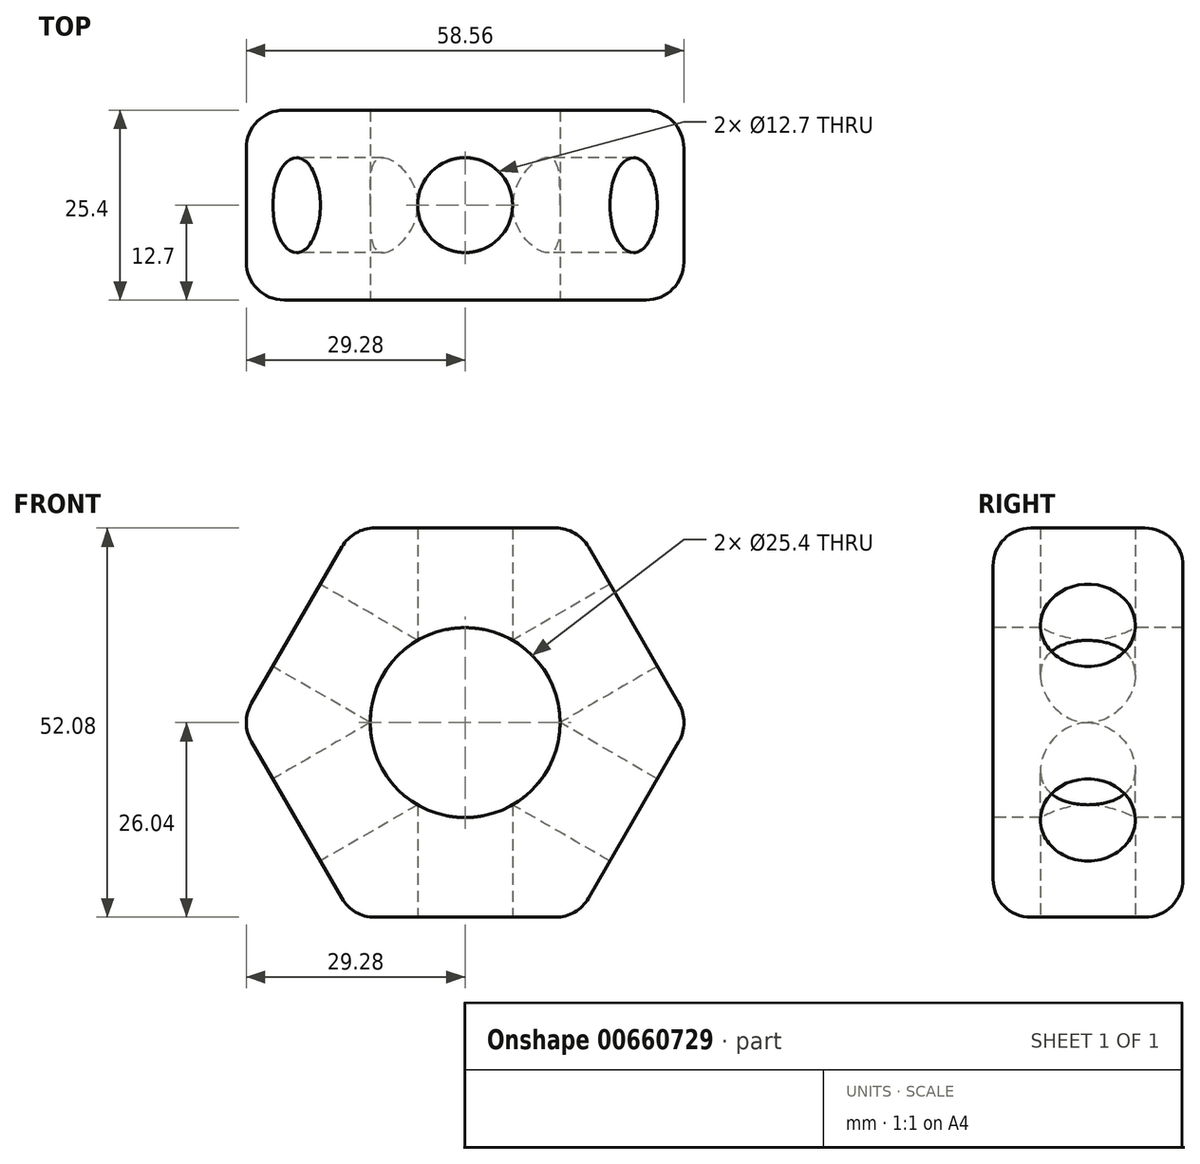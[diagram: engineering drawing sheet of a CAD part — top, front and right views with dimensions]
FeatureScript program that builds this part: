
annotation { "Feature Type Name" : "Feature", "Feature Type Description" : "" }
export const myFeature = defineFeature(function(context is Context, id is Id, definition is map)
    precondition{}
    {
        {
            var Q0;
            Q0=qCreatedBy(makeId("Front.planeOp"),FACE);
            var sketch = newSketch(context, id + "F0", { "sketchPlane" : qUnion([Q0])});
            skCircle(sketch, "E0", {"center": v(0, 0) * mm, "radius": 26.04 * mm});
            skCircle(sketch, "E1.cCircle", {"center": v(0, 0) * mm, "radius": 26.04 * mm, "construction": true});
            skLineSegment(sketch, "E1.0", {"start": v(-15.03, 26.04) * mm, "end": v(15.03, 26.04) * mm});
            skLineSegment(sketch, "E1.1", {"start": v(15.03, 26.04) * mm, "end": v(30.07, 0) * mm});
            skLineSegment(sketch, "E1.2", {"start": v(30.07, 0) * mm, "end": v(15.03, -26.04) * mm});
            skLineSegment(sketch, "E1.3", {"start": v(15.03, -26.04) * mm, "end": v(-15.03, -26.04) * mm});
            skLineSegment(sketch, "E1.4", {"start": v(-15.03, -26.04) * mm, "end": v(-30.07, 0) * mm});
            skLineSegment(sketch, "E1.5", {"start": v(-30.07, 0) * mm, "end": v(-15.03, 26.04) * mm});
            skPoint(sketch, "E1.0.midPoint", {"position": v(0, 26.04) * mm});
            skSolve(sketch);
        }
        {
            var Q0;
            Q0 = qSketchRegion(id + "F0", true);
            extrude(context, id + "F1", {"entities" : qUnion([Q0]), "endBound" : BoundingType.SYMMETRIC, "depth" : 25.4 * mm, "offsetDistance" : 25.4 * mm});
        }
        {
            var Q0;
            Q0=qCreatedBy(makeId("Front.planeOp"),FACE);
            var sketch = newSketch(context, id + "F2", { "sketchPlane" : qUnion([Q0])});
            skCircle(sketch, "E2", {"center": v(0, 0) * mm, "radius": 11.03 * mm});
            skSolve(sketch);
        }
        {
            var Q0;
            Q0=qCreatedBy(makeId("Front.planeOp"),FACE);
            var sketch = newSketch(context, id + "F3", { "sketchPlane" : qUnion([Q0])});
            skCircle(sketch, "E3", {"center": v(0, 0) * mm, "radius": 1.4 * mm});
            skSolve(sketch);
        }
        {
            var Q0;
            Q0=sQuery(id+"F3.wireOp",VERTEX,"E3.center");
            var Q1;
            Q1=makeQuery(id+"F1.opExtrude","SWEPT_BODY",BODY,{"disambiguationData":[OSD([sQuery(id+"F0.wireOp",EDGE,"E1.0"),sQuery(id+"F0.wireOp",EDGE,"E1.1"),sQuery(id+"F0.wireOp",EDGE,"E1.2"),sQuery(id+"F0.wireOp",EDGE,"E1.3"),sQuery(id+"F0.wireOp",EDGE,"E1.4"),sQuery(id+"F0.wireOp",EDGE,"E1.5")])]});
            hole(context, id + "F4", {"style" : HoleStyle.SIMPLE, "endStyle" : HoleEndStyle.THROUGH, "holeDiameter" : 25.4 * mm, "majorDiameter" : 6.35 * mm, "isTappedThrough" : true, "tappedDepth" : 12.7 * mm, "tapClearance" : 3, "locations" : qUnion([Q0]), "scope" : qUnion([Q1])});
        }
        {
            var Q0;
            Q0=sQuery(id+"F2.wireOp",VERTEX,"E2.center");
            var Q1;
            Q1=makeQuery(id+"F1.opExtrude","SWEPT_BODY",BODY,{"disambiguationData":[OSD([sQuery(id+"F0.wireOp",EDGE,"E1.0"),sQuery(id+"F0.wireOp",EDGE,"E1.1"),sQuery(id+"F0.wireOp",EDGE,"E1.2"),sQuery(id+"F0.wireOp",EDGE,"E1.3"),sQuery(id+"F0.wireOp",EDGE,"E1.4"),sQuery(id+"F0.wireOp",EDGE,"E1.5")])]});
            hole(context, id + "F5", {"style" : HoleStyle.SIMPLE, "endStyle" : HoleEndStyle.THROUGH, "oppositeDirection" : true, "holeDiameter" : 25.4 * mm, "majorDiameter" : 6.35 * mm, "isTappedThrough" : true, "tappedDepth" : 12.7 * mm, "tapClearance" : 3, "locations" : qUnion([Q0]), "scope" : qUnion([Q1])});
        }
        {
            var Q0;
            Q0=makeQuery(id+"F1.opExtrude","SWEPT_FACE",FACE,{"disambiguationData":[OSD([sQuery(id+"F0.wireOp",EDGE,"E1.5")])]});
            var sketch = newSketch(context, id + "F6", { "sketchPlane" : qUnion([Q0])});
            skPoint(sketch, "E4", {"position": v(0, 0) * mm});
            skSolve(sketch);
        }
        {
            var Q0;
            Q0=sQuery(id+"F6.wireOp",VERTEX,"E4");
            var Q1;
            Q1=makeQuery(id+"F1.opExtrude","SWEPT_BODY",BODY,{"disambiguationData":[OSD([sQuery(id+"F0.wireOp",EDGE,"E1.0"),sQuery(id+"F0.wireOp",EDGE,"E1.1"),sQuery(id+"F0.wireOp",EDGE,"E1.2"),sQuery(id+"F0.wireOp",EDGE,"E1.3"),sQuery(id+"F0.wireOp",EDGE,"E1.4"),sQuery(id+"F0.wireOp",EDGE,"E1.5")])]});
            hole(context, id + "F7", {"style" : HoleStyle.SIMPLE, "endStyle" : HoleEndStyle.THROUGH, "holeDiameter" : 12.7 * mm, "majorDiameter" : 5 * mm, "isTappedThrough" : true, "tappedDepth" : 12.7 * mm, "tapClearance" : 3, "locations" : qUnion([Q0]), "scope" : qUnion([Q1])});
        }
        {
            var Q0;
            Q0=makeQuery(id+"F1.opExtrude","SWEPT_EDGE",EDGE,{"disambiguationData":[OSD([sQuery(id+"F0.wireOp",EDGE,"E1.4"),sQuery(id+"F0.wireOp",EDGE,"E1.5")])]});
            fillet(context, id + "F8", {"entities" : qUnion([Q0]), "radius" : 5.08 * mm, "tangentPropagation" : true, "allowEdgeOverflow" : false});
        }
        {
            var Q0;
            Q0=makeQuery(id+"F1.opExtrude","SWEPT_EDGE",EDGE,{"disambiguationData":[OSD([sQuery(id+"F0.wireOp",EDGE,"E1.3"),sQuery(id+"F0.wireOp",EDGE,"E1.4")])]});
            var Q1;
            Q1=makeQuery(id+"F1.opExtrude","SWEPT_EDGE",EDGE,{"disambiguationData":[OSD([sQuery(id+"F0.wireOp",EDGE,"E1.0"),sQuery(id+"F0.wireOp",EDGE,"E1.5")])]});
            var Q2;
            Q2=makeQuery(id+"F1.opExtrude","SWEPT_EDGE",EDGE,{"disambiguationData":[OSD([sQuery(id+"F0.wireOp",EDGE,"E1.2"),sQuery(id+"F0.wireOp",EDGE,"E1.3")])]});
            var Q3;
            Q3=makeQuery(id+"F1.opExtrude","SWEPT_EDGE",EDGE,{"disambiguationData":[OSD([sQuery(id+"F0.wireOp",EDGE,"E1.1"),sQuery(id+"F0.wireOp",EDGE,"E1.2")])]});
            var Q4;
            Q4=makeQuery(id+"F1.opExtrude","SWEPT_EDGE",EDGE,{"disambiguationData":[OSD([sQuery(id+"F0.wireOp",EDGE,"E1.0"),sQuery(id+"F0.wireOp",EDGE,"E1.1")])]});
            fillet(context, id + "F9", {"entities" : qUnion([Q0, Q1, Q2, Q3, Q4]), "radius" : 5.08 * mm, "tangentPropagation" : true, "allowEdgeOverflow" : false});
        }
        {
            var Q0;
            Q0=makeQuery(id+"F9.opFillet","BLEND_FACE",FACE,{"disambiguationData":[OSD([sQuery(id+"F0.wireOp",EDGE,"E1.1"),sQuery(id+"F0.wireOp",EDGE,"E1.2")])]});
            fillet(context, id + "F10", {"entities" : qUnion([Q0]), "radius" : 5.08 * mm, "tangentPropagation" : true, "allowEdgeOverflow" : false});
        }
        {
            var Q0;
            Q0=makeQuery(id+"F1.opExtrude","SWEPT_FACE",FACE,{"disambiguationData":[OSD([sQuery(id+"F0.wireOp",EDGE,"E1.4")])]});
            var sketch = newSketch(context, id + "F11", { "sketchPlane" : qUnion([Q0])});
            skPoint(sketch, "E5", {"position": v(0, 0) * mm});
            skSolve(sketch);
        }
        {
            var Q0;
            Q0=sQuery(id+"F11.wireOp",VERTEX,"E5");
            var Q1;
            Q1=makeQuery(id+"F1.opExtrude","SWEPT_BODY",BODY,{"disambiguationData":[OSD([sQuery(id+"F0.wireOp",EDGE,"E1.0"),sQuery(id+"F0.wireOp",EDGE,"E1.1"),sQuery(id+"F0.wireOp",EDGE,"E1.2"),sQuery(id+"F0.wireOp",EDGE,"E1.3"),sQuery(id+"F0.wireOp",EDGE,"E1.4"),sQuery(id+"F0.wireOp",EDGE,"E1.5")])]});
            hole(context, id + "F12", {"style" : HoleStyle.SIMPLE, "endStyle" : HoleEndStyle.THROUGH, "holeDiameter" : 12.7 * mm, "majorDiameter" : 6.35 * mm, "isTappedThrough" : true, "tappedDepth" : 12.7 * mm, "tapClearance" : 3, "locations" : qUnion([Q0]), "scope" : qUnion([Q1])});
        }
        {
            var Q0;
            Q0=makeQuery(id+"F1.opExtrude","SWEPT_FACE",FACE,{"disambiguationData":[OSD([sQuery(id+"F0.wireOp",EDGE,"E1.3")])]});
            var sketch = newSketch(context, id + "F13", { "sketchPlane" : qUnion([Q0])});
            skPoint(sketch, "E6", {"position": v(0, 0) * mm});
            skSolve(sketch);
        }
        {
            var Q0;
            Q0=sQuery(id+"F13.wireOp",VERTEX,"E6");
            var Q1;
            Q1=makeQuery(id+"F1.opExtrude","SWEPT_BODY",BODY,{"disambiguationData":[OSD([sQuery(id+"F0.wireOp",EDGE,"E1.0"),sQuery(id+"F0.wireOp",EDGE,"E1.1"),sQuery(id+"F0.wireOp",EDGE,"E1.2"),sQuery(id+"F0.wireOp",EDGE,"E1.3"),sQuery(id+"F0.wireOp",EDGE,"E1.4"),sQuery(id+"F0.wireOp",EDGE,"E1.5")])]});
            hole(context, id + "F14", {"style" : HoleStyle.SIMPLE, "endStyle" : HoleEndStyle.THROUGH, "holeDiameter" : 12.7 * mm, "majorDiameter" : 6.35 * mm, "isTappedThrough" : true, "tappedDepth" : 12.7 * mm, "tapClearance" : 3, "locations" : qUnion([Q0]), "scope" : qUnion([Q1])});
        }
    });
